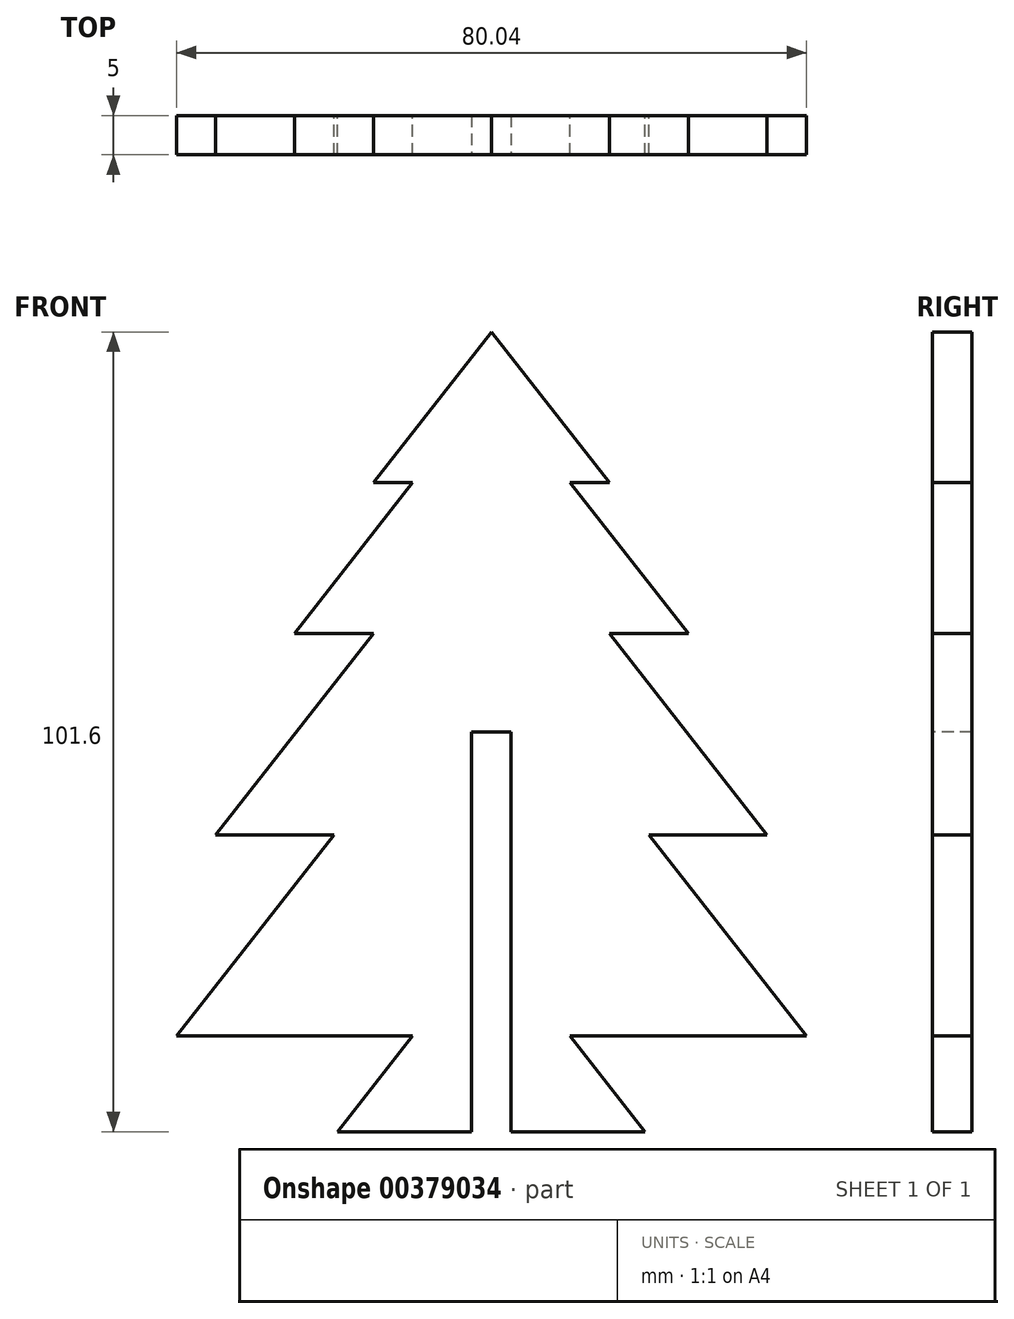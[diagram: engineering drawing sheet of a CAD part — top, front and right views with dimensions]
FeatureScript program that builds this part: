
annotation { "Feature Type Name" : "Feature", "Feature Type Description" : "" }
export const myFeature = defineFeature(function(context is Context, id is Id, definition is map)
    precondition{}
    {
        {
            var Q0;
            Q0=qCreatedBy(makeId("Front.planeOp"),FACE);
            var sketch = newSketch(context, id + "F0", { "sketchPlane" : qUnion([Q0])});
            skLineSegment(sketch, "E0", {"start": v(-20.58, -21.79) * mm, "end": v(-10.58, -21.79) * mm});
            skLineSegment(sketch, "E1", {"start": v(-10.58, -21.79) * mm, "end": v(-30.59, -21.79) * mm});
            skLineSegment(sketch, "E2", {"start": v(-30.59, -21.79) * mm, "end": v(-30.59, -9.62) * mm});
            skLineSegment(sketch, "E3", {"start": v(-10.58, -9.62) * mm, "end": v(-30.59, -9.62) * mm});
            skLineSegment(sketch, "E4", {"start": v(-10.58, -9.62) * mm, "end": v(-10.58, -21.79) * mm});
            skLineSegment(sketch, "E5", {"start": v(-20.58, -21.79) * mm, "end": v(-20.58, -9.62) * mm});
            skLineSegment(sketch, "E6", {"start": v(-30.59, -9.62) * mm, "end": v(-60.6, -9.62) * mm});
            skLineSegment(sketch, "E7", {"start": v(-10.58, -9.62) * mm, "end": v(19.44, -9.62) * mm});
            skLineSegment(sketch, "E8", {"start": v(-60.6, -9.62) * mm, "end": v(-40.6, 15.93) * mm});
            skLineSegment(sketch, "E9", {"start": v(-40.6, 15.93) * mm, "end": v(-0.57, 15.93) * mm});
            skLineSegment(sketch, "E10", {"start": v(-0.57, 15.93) * mm, "end": v(19.44, -9.62) * mm});
            skLineSegment(sketch, "E11", {"start": v(-20.58, -9.62) * mm, "end": v(-20.58, 15.93) * mm});
            skLineSegment(sketch, "E12", {"start": v(-40.6, 15.93) * mm, "end": v(-55.6, 15.93) * mm});
            skLineSegment(sketch, "E13", {"start": v(-55.6, 15.93) * mm, "end": v(-35.6, 41.49) * mm});
            skLineSegment(sketch, "E14", {"start": v(-0.57, 15.93) * mm, "end": v(14.43, 15.93) * mm});
            skLineSegment(sketch, "E15", {"start": v(14.43, 15.93) * mm, "end": v(-5.58, 41.49) * mm});
            skLineSegment(sketch, "E16", {"start": v(-5.58, 41.49) * mm, "end": v(-35.6, 41.49) * mm});
            skLineSegment(sketch, "E17", {"start": v(-20.58, 15.93) * mm, "end": v(-20.58, 41.49) * mm});
            skLineSegment(sketch, "E18", {"start": v(-35.6, 41.49) * mm, "end": v(-45.6, 41.49) * mm});
            skLineSegment(sketch, "E19", {"start": v(-45.6, 41.49) * mm, "end": v(-30.59, 60.65) * mm});
            skLineSegment(sketch, "E20", {"start": v(-30.59, 60.65) * mm, "end": v(-10.58, 60.65) * mm});
            skLineSegment(sketch, "E21", {"start": v(-10.58, 60.65) * mm, "end": v(4.43, 41.49) * mm});
            skLineSegment(sketch, "E22", {"start": v(4.43, 41.49) * mm, "end": v(-5.58, 41.49) * mm});
            skLineSegment(sketch, "E23", {"start": v(-30.59, 60.65) * mm, "end": v(-35.6, 60.65) * mm});
            skLineSegment(sketch, "E24", {"start": v(-35.6, 60.65) * mm, "end": v(-20.58, 79.81) * mm});
            skLineSegment(sketch, "E25", {"start": v(-20.58, 79.81) * mm, "end": v(-5.58, 60.65) * mm});
            skLineSegment(sketch, "E26", {"start": v(-5.58, 60.65) * mm, "end": v(-10.58, 60.65) * mm});
            skLineSegment(sketch, "E27", {"start": v(-60.6, -9.62) * mm, "end": v(-20.58, -9.62) * mm});
            skLineSegment(sketch, "E28", {"start": v(-20.58, -9.62) * mm, "end": v(19.44, -9.62) * mm});
            skLineSegment(sketch, "E29", {"start": v(-30.59, -21.79) * mm, "end": v(-40.12, -21.79) * mm});
            skLineSegment(sketch, "E30", {"start": v(-40.12, -21.79) * mm, "end": v(-30.59, -9.62) * mm});
            skLineSegment(sketch, "E31", {"start": v(-10.58, -21.79) * mm, "end": v(-1.05, -21.79) * mm});
            skLineSegment(sketch, "E32", {"start": v(-1.05, -21.79) * mm, "end": v(-10.58, -9.62) * mm});
            skSolve(sketch);
        }
        {
            var Q0;
            Q0 = qSketchRegion(id + "F0", true);
            extrude(context, id + "F1", {"entities" : qUnion([Q0]), "depth" : 5 * mm});
        }
        {
            var Q0;
            Q0=makeQuery(id+"F1.opExtrude","CAP_FACE",FACE,{"disambiguationData":[OSD([sQuery(id+"F0.wireOp",EDGE,"E1"),sQuery(id+"F0.wireOp",EDGE,"E8"),sQuery(id+"F0.wireOp",EDGE,"E10"),sQuery(id+"F0.wireOp",EDGE,"E12"),sQuery(id+"F0.wireOp",EDGE,"E13"),sQuery(id+"F0.wireOp",EDGE,"E14"),sQuery(id+"F0.wireOp",EDGE,"E15"),sQuery(id+"F0.wireOp",EDGE,"E18"),sQuery(id+"F0.wireOp",EDGE,"E19"),sQuery(id+"F0.wireOp",EDGE,"E21"),sQuery(id+"F0.wireOp",EDGE,"E22"),sQuery(id+"F0.wireOp",EDGE,"E23"),sQuery(id+"F0.wireOp",EDGE,"E24"),sQuery(id+"F0.wireOp",EDGE,"E25"),sQuery(id+"F0.wireOp",EDGE,"E26"),sQuery(id+"F0.wireOp",EDGE,"E27"),sQuery(id+"F0.wireOp",EDGE,"E28"),sQuery(id+"F0.wireOp",EDGE,"E29"),sQuery(id+"F0.wireOp",EDGE,"E30"),sQuery(id+"F0.wireOp",EDGE,"E31"),sQuery(id+"F0.wireOp",EDGE,"E32")])],"isStart":false});
            var sketch = newSketch(context, id + "F2", { "sketchPlane" : qUnion([Q0])});
            skLineSegment(sketch, "E33", {"start": v(-20.58, -21.79) * mm, "end": v(-20.58, 29.01) * mm});
            skLineSegment(sketch, "E34.bottom", {"start": v(-18.08, -21.79) * mm, "end": v(-23.08, -21.79) * mm});
            skLineSegment(sketch, "E34.top", {"start": v(-18.08, 29.01) * mm, "end": v(-23.08, 29.01) * mm});
            skLineSegment(sketch, "E34.left", {"start": v(-18.08, -21.79) * mm, "end": v(-18.08, 29.01) * mm});
            skLineSegment(sketch, "E34.right", {"start": v(-23.08, -21.79) * mm, "end": v(-23.08, 29.01) * mm});
            skPoint(sketch, "E34.middle", {"position": v(-20.58, 3.61) * mm});
            skSolve(sketch);
        }
        {
            var Q0;
            {var subQ0=sQuery(id+"F2.wireOp",EDGE,"E33");Q0=makeQuery(id+"F2.imprint","IMPRINT",FACE,{"disambiguationData":[TD([[makeQuery(id+"F2.imprint","IMPRINT",EDGE,{"derivedFrom":subQ0}),1.0]])]});}
            var Q1;
            {var subQ0=sQuery(id+"F2.wireOp",EDGE,"E33");Q1=makeQuery(id+"F2.imprint","IMPRINT",FACE,{"disambiguationData":[TD([[makeQuery(id+"F2.imprint","IMPRINT",EDGE,{"derivedFrom":subQ0}),-1.0]])]});}
            extrude(context, id + "F3", {"entities" : qUnion([Q0, Q1]), "operationType" : NewBodyOperationType.REMOVE, "oppositeDirection" : true, "depth" : 25 * mm});
        }
    });
